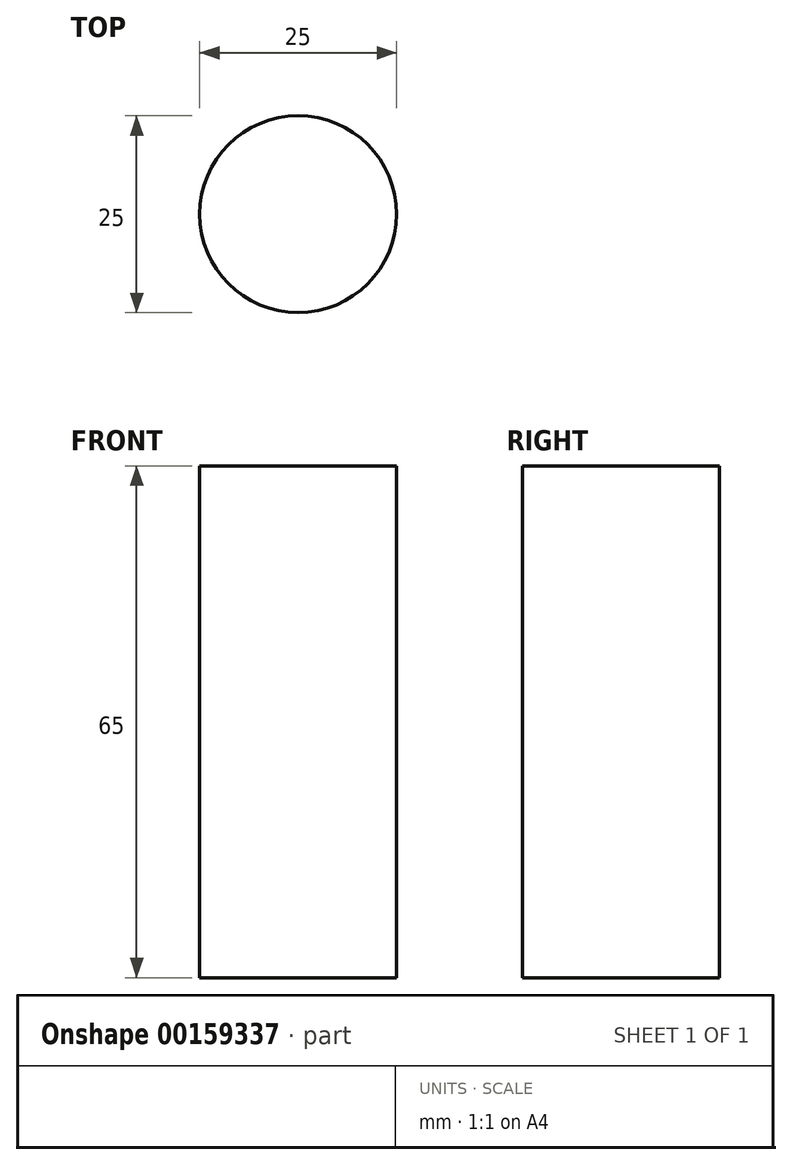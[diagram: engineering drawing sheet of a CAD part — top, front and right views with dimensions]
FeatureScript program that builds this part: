
annotation { "Feature Type Name" : "Feature", "Feature Type Description" : "" }
export const myFeature = defineFeature(function(context is Context, id is Id, definition is map)
    precondition{}
    {
        {
            var Q0;
            Q0=qCreatedBy(makeId("Top.planeOp"),FACE);
            var sketch = newSketch(context, id + "F0", { "sketchPlane" : qUnion([Q0])});
            skCircle(sketch, "E0", {"center": v(0, 0) * mm, "radius": 12.5 * mm});
            skSolve(sketch);
        }
        {
            var Q0;
            Q0 = qSketchRegion(id + "F0", true);
            extrude(context, id + "F1", {"entities" : qUnion([Q0]), "depth" : 65 * mm});
        }
    });
